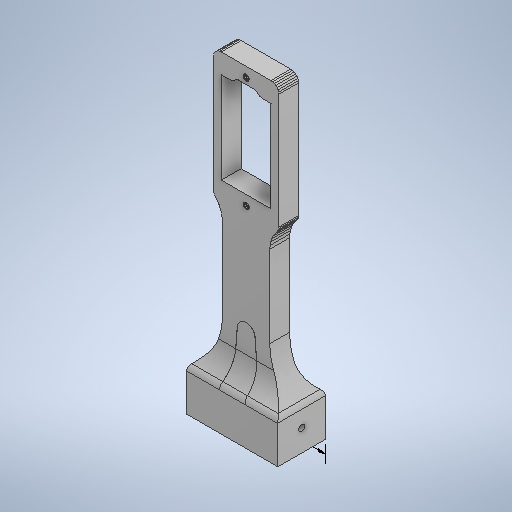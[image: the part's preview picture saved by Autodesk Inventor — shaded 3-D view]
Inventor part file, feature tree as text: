
AUTODESK INVENTOR PART (.ipt)
format: ipt  version: 2025 (Build 290162000, 162)  size: 669,696 bytes
history: native  units: in
note: dims shown in document units (in); Inventor stores cm internally (conversion verified against a paired STEP export)
features: fillet x12, other x5, sketch x3, extrude x2, thicken_offset x1, direct_edit x1, hole x1
ambient origin geometry x8: Origin, YZ Plane, XZ Plane, XY Plane, X Axis, Y Axis, Z Axis, Center Point
bodies: Solid1 (feature_tree)
feature tree (25):
  other  "ogniwo1_"
  other  "Annotations"
  other  "MeshFeature1"
  sketch  "Sketch1"  dims[d2=1.9685in d3=1.9685in d4=1.9685in d5=2.9921in d6=0.0in d7=0.0in]
  thicken_offset  "Thicken2"
  extrude  "Extrusion1"  Depth=1.9685in TaperAngle=0.0deg
  extrude  "Extrusion2"  Depth=11.5157in
  fillet  "Fillet1"  Radius=10.4331in
  fillet  "Fillet2"  Radius=3.5in
  fillet  "Fillet3"  Radius=15.748in
  fillet  "Fillet4"  Radius=15.748in
  fillet  "Fillet5"  Radius=8.5in
  direct_edit  "Direct Edit1"
  fillet  "Fillet6"  Radius=7.874in
  fillet  "Fillet7"  Radius=7.874in
  fillet  "Fillet8"  Radius=7.874in
  fillet  "Fillet9"  Radius=0.3071in
  fillet  "Fillet10"  Radius=0.0787in
  fillet  "Fillet11"  Radius=0.0787in
  fillet  "Fillet12"  Radius=0.0787in
  hole  "Hole1"  [1 undecoded]
  sketch  "Sketch4"  dims[d9=11.5157in d10=11.5157in d11=10.4331in d12=3.5in d13=0.0in d14=15.748in d15=15.748in d16=8.5in d17=0.0in d18=7.874in d19=7.874in d20=7.874in]
  sketch  "Sketch5"  dims[d24=0.0155in d25=0.3937in d26=0.3937in d27=0.3071in d28=0.0787in d29=0.0787in d30=0.0787in d31=0.0787in d32=0.0787in d33=0.0787in d34=0.0591in d35=0.0591in d36=0.2362in d37=0.1575in d38=0.0787in d39=90.0deg d40=0.315in d41=0.8108in d21=0.2214in d22=0.2044in d23=0.9055in]
  other  "Scale1"
  other  "Linear Dimension 1"
note: 1 required parameter value undecoded (feature->parameter linkage not recoverable at this tier; creation-order binding heuristic only, values carry confidence <= 0.55)
